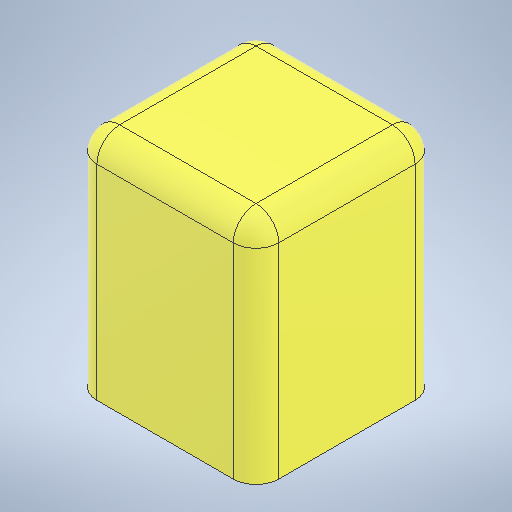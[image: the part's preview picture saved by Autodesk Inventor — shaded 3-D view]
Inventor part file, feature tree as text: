
AUTODESK INVENTOR PART (.ipt)
format: ipt  version: 2025.2 (Build 292293000, 293)  size: 229,888 bytes
history: native  units: mm
features: other x1, extrude x1, fillet x1, sketch x1
ambient origin geometry x8: Origin, YZ Plane, XZ Plane, XY Plane, X Axis, Y Axis, Z Axis, Center Point
bodies: Body1 (feature_tree)
feature tree (4):
  other  "Sólido1"
  extrude  "Extrusión1"  Depth=400.0mm
  fillet  "Empalme1"  Radius=500.0mm
  sketch  "Boceto1"  dims[d0=400.0mm d1=400.0mm d2=500.0mm d3=0.0mm d4=50.0mm]
